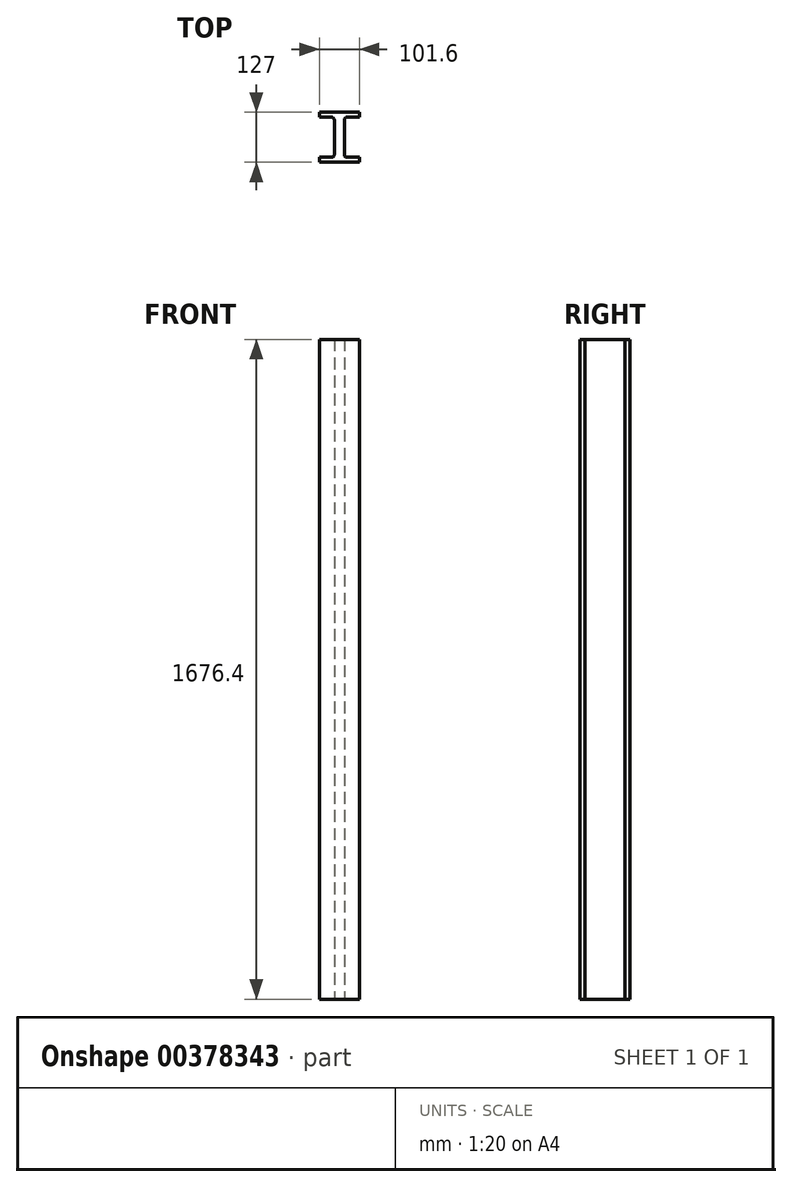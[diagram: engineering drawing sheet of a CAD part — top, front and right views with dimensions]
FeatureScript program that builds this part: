
annotation { "Feature Type Name" : "Feature", "Feature Type Description" : "" }
export const myFeature = defineFeature(function(context is Context, id is Id, definition is map)
    precondition{}
    {
        {
            var Q0;
            Q0=qCreatedBy(makeId("Top.planeOp"),FACE);
            var sketch = newSketch(context, id + "F0", { "sketchPlane" : qUnion([Q0])});
            skPoint(sketch, "E0", {"position": v(0, 0) * mm});
            skPoint(sketch, "E1", {"position": v(609.18, 292.38) * mm});
            skPoint(sketch, "E2", {"position": v(0, 63.5) * mm});
            skPoint(sketch, "E3", {"position": v(0, -63.5) * mm});
            skPoint(sketch, "E4", {"position": v(12.7, 63.5) * mm});
            skLineSegment(sketch, "E5.bottom", {"start": v(12.7, 63.5) * mm, "end": v(-12.7, 63.5) * mm});
            skLineSegment(sketch, "E5.top", {"start": v(12.7, -63.5) * mm, "end": v(-12.7, -63.5) * mm});
            skLineSegment(sketch, "E5.left", {"start": v(12.7, 63.5) * mm, "end": v(12.7, -63.5) * mm});
            skLineSegment(sketch, "E5.right", {"start": v(-12.7, 63.5) * mm, "end": v(-12.7, -63.5) * mm});
            skPoint(sketch, "E6", {"position": v(0, 57.15) * mm});
            skPoint(sketch, "E7", {"position": v(50.8, 63.5) * mm});
            skLineSegment(sketch, "E8.bottom", {"start": v(50.8, 63.5) * mm, "end": v(-50.8, 63.5) * mm});
            skLineSegment(sketch, "E8.top", {"start": v(50.8, 50.8) * mm, "end": v(-50.8, 50.8) * mm});
            skLineSegment(sketch, "E8.left", {"start": v(50.8, 63.5) * mm, "end": v(50.8, 50.8) * mm});
            skLineSegment(sketch, "E8.right", {"start": v(-50.8, 63.5) * mm, "end": v(-50.8, 50.8) * mm});
            skLineSegment(sketch, "E9", {"start": v(12.7, 0) * mm, "end": v(-12.7, 0) * mm, "construction": true});
            skLineSegment(sketch, "E10.MirrorCS", {"start": v(50.8, -50.8) * mm, "end": v(-50.8, -50.8) * mm});
            skLineSegment(sketch, "E11.MirrorCS", {"start": v(50.8, -63.5) * mm, "end": v(-50.8, -63.5) * mm});
            skPoint(sketch, "E12.MirrorP", {"position": v(50.8, -63.5) * mm});
            skLineSegment(sketch, "E13.MirrorCS", {"start": v(50.8, -63.5) * mm, "end": v(50.8, -50.8) * mm});
            skLineSegment(sketch, "E14.MirrorCS", {"start": v(-50.8, -63.5) * mm, "end": v(-50.8, -50.8) * mm});
            skSolve(sketch);
        }
        {
            var Q0;
            {var subQ0=sQuery(id+"F0.wireOp",EDGE,"E11.MirrorCS");var subQ1=sQuery(id+"F0.wireOp",EDGE,"E5.left");var subQ2=makeQuery(id+"F0.imprint","INTERSECT",VERTEX,{"derivedFrom":[subQ1,subQ0]});Q0=makeQuery(id+"F0.imprint","IMPRINT",FACE,{"disambiguationData":[TD([[makeQuery(id+"F0.imprint","IMPRINT",EDGE,{"disambiguationData":[TD([[subQ2,1.0]])],"derivedFrom":subQ1}),-1.0]])]});}
            var Q1;
            {var subQ5=sQuery(id+"F0.wireOp",EDGE,"E13.MirrorCS");Q1=makeQuery(id+"F0.imprint","IMPRINT",FACE,{"disambiguationData":[TD([[makeQuery(id+"F0.imprint","IMPRINT",EDGE,{"derivedFrom":subQ5}),1.0]])]});}
            var Q2;
            {var subQ5=sQuery(id+"F0.wireOp",EDGE,"E14.MirrorCS");Q2=makeQuery(id+"F0.imprint","IMPRINT",FACE,{"disambiguationData":[TD([[makeQuery(id+"F0.imprint","IMPRINT",EDGE,{"derivedFrom":subQ5}),-1.0]])]});}
            var Q3;
            {var subQ0=sQuery(id+"F0.wireOp",EDGE,"E8.top");var subQ1=sQuery(id+"F0.wireOp",EDGE,"E5.left");var subQ2=makeQuery(id+"F0.imprint","INTERSECT",VERTEX,{"derivedFrom":[subQ1,subQ0]});Q3=makeQuery(id+"F0.imprint","IMPRINT",FACE,{"disambiguationData":[TD([[makeQuery(id+"F0.imprint","IMPRINT",EDGE,{"disambiguationData":[TD([[subQ2,-1.0]])],"derivedFrom":subQ1}),-1.0]])]});}
            var Q4;
            {var subQ5=sQuery(id+"F0.wireOp",EDGE,"E8.left");Q4=makeQuery(id+"F0.imprint","IMPRINT",FACE,{"disambiguationData":[TD([[makeQuery(id+"F0.imprint","IMPRINT",EDGE,{"derivedFrom":subQ5}),-1.0]])]});}
            var Q5;
            {var subQ0=sQuery(id+"F0.wireOp",EDGE,"E8.bottom");var subQ1=sQuery(id+"F0.wireOp",EDGE,"E5.left");var subQ2=makeQuery(id+"F0.imprint","INTERSECT",VERTEX,{"derivedFrom":[subQ1,subQ0]});Q5=makeQuery(id+"F0.imprint","IMPRINT",FACE,{"disambiguationData":[TD([[makeQuery(id+"F0.imprint","IMPRINT",EDGE,{"disambiguationData":[TD([[subQ2,-1.0]])],"derivedFrom":subQ1}),-1.0]])]});}
            var Q6;
            {var subQ5=sQuery(id+"F0.wireOp",EDGE,"E8.right");Q6=makeQuery(id+"F0.imprint","IMPRINT",FACE,{"disambiguationData":[TD([[makeQuery(id+"F0.imprint","IMPRINT",EDGE,{"derivedFrom":subQ5}),1.0]])]});}
            extrude(context, id + "F1", {"entities" : qUnion([Q0, Q1, Q2, Q3, Q4, Q5, Q6]), "depth" : 1676.4 * mm});
        }
        {
            var Q0;
            Q0=makeQuery(id+"F1.opExtrude","SWEPT_EDGE",EDGE,{"disambiguationData":[OSD([sQuery(id+"F0.wireOp",EDGE,"E5.right"),sQuery(id+"F0.wireOp",EDGE,"E10.MirrorCS")])]});
            var Q1;
            Q1=makeQuery(id+"F1.opExtrude","SWEPT_EDGE",EDGE,{"disambiguationData":[OSD([sQuery(id+"F0.wireOp",EDGE,"E5.left"),sQuery(id+"F0.wireOp",EDGE,"E10.MirrorCS")])]});
            var Q2;
            Q2=makeQuery(id+"F1.opExtrude","SWEPT_EDGE",EDGE,{"disambiguationData":[OSD([sQuery(id+"F0.wireOp",EDGE,"E5.right"),sQuery(id+"F0.wireOp",EDGE,"E8.top")])]});
            var Q3;
            Q3=makeQuery(id+"F1.opExtrude","SWEPT_EDGE",EDGE,{"disambiguationData":[OSD([sQuery(id+"F0.wireOp",EDGE,"E5.left"),sQuery(id+"F0.wireOp",EDGE,"E8.top")])]});
            fillet(context, id + "F2", {"entities" : qUnion([Q0, Q1, Q2, Q3]), "radius" : 6.35 * mm, "tangentPropagation" : true, "allowEdgeOverflow" : false});
        }
    });
